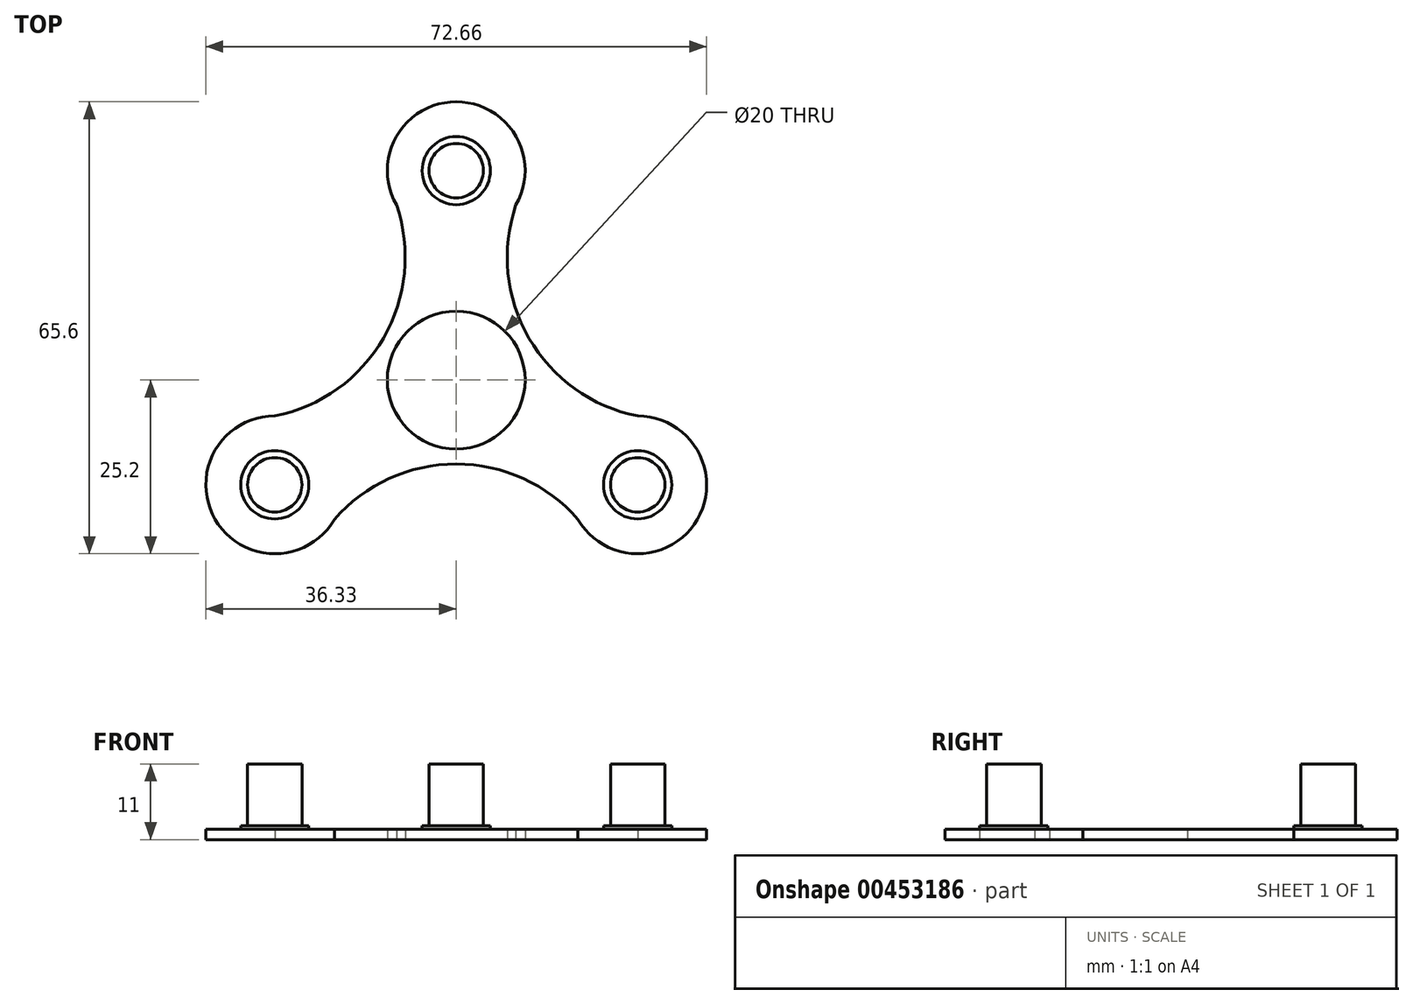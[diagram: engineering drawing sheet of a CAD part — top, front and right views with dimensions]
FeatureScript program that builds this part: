
annotation { "Feature Type Name" : "Feature", "Feature Type Description" : "" }
export const myFeature = defineFeature(function(context is Context, id is Id, definition is map)
    precondition{}
    {
        {
            var Q0;
            Q0=qCreatedBy(makeId("Top.planeOp"),FACE);
            var sketch = newSketch(context, id + "F0", { "sketchPlane" : qUnion([Q0])});
            skCircle(sketch, "E0", {"center": v(0, 0) * mm, "radius": 10 * mm});
            skLineSegment(sketch, "E1", {"start": v(0, 0) * mm, "end": v(0, 30.4) * mm});
            skCircle(sketch, "E2", {"center": v(0, 30.4) * mm, "radius": 3.95 * mm});
            skCircle(sketch, "E3.0", {"center": v(0, 30.4) * mm, "radius": 4.95 * mm});
            skCircle(sketch, "E4", {"center": v(0, 30.4) * mm, "radius": 10 * mm});
            skLineSegment(sketch, "E5", {"start": v(0, 30.4) * mm, "end": v(-8.66, 25.4) * mm});
            skLineSegment(sketch, "E6.MirrorCS", {"start": v(0, 30.4) * mm, "end": v(8.66, 25.4) * mm});
            skCircle(sketch, "E7.1.0", {"center": v(26.33, -15.2) * mm, "radius": 3.95 * mm});
            skLineSegment(sketch, "E7.1.1", {"start": v(26.33, -15.2) * mm, "end": v(17.67, -20.2) * mm});
            skLineSegment(sketch, "E7.1.2", {"start": v(26.33, -15.2) * mm, "end": v(26.33, -5.2) * mm});
            skCircle(sketch, "E7.1.3", {"center": v(26.33, -15.2) * mm, "radius": 4.95 * mm});
            skCircle(sketch, "E7.1.4", {"center": v(26.33, -15.2) * mm, "radius": 10 * mm});
            skCircle(sketch, "E7.2.0", {"center": v(-26.33, -15.2) * mm, "radius": 3.95 * mm});
            skLineSegment(sketch, "E7.2.1", {"start": v(-26.33, -15.2) * mm, "end": v(-26.33, -5.2) * mm});
            skLineSegment(sketch, "E7.2.2", {"start": v(-26.33, -15.2) * mm, "end": v(-17.67, -20.2) * mm});
            skCircle(sketch, "E7.2.3", {"center": v(-26.33, -15.2) * mm, "radius": 4.95 * mm});
            skCircle(sketch, "E7.2.4", {"center": v(-26.33, -15.2) * mm, "radius": 10 * mm});
            skLineSegment(sketch, "E7.anchor1", {"start": v(0, 0) * mm, "end": v(-8.66, 25.4) * mm, "construction": true});
            skLineSegment(sketch, "E7.anchor2", {"start": v(0, 0) * mm, "end": v(-17.67, -20.2) * mm, "construction": true});
            skArc(sketch, "E8", {"start": v(-26.33, -5.2) * mm, "mid": v(-10.55, 6.1) * mm, "end": v(-8.66, 25.4) * mm});
            skArc(sketch, "E9.1.0", {"start": v(17.67, -20.2) * mm, "mid": v(0, -12.18) * mm, "end": v(-17.67, -20.2) * mm});
            skArc(sketch, "E9.2.0", {"start": v(8.66, 25.4) * mm, "mid": v(10.55, 6.1) * mm, "end": v(26.33, -5.2) * mm});
            skSolve(sketch);
        }
        {
            var Q0;
            {var subQ0=sQuery(id+"F0.wireOp",EDGE,"E5");var subQ1=sQuery(id+"F0.wireOp",EDGE,"E3.0");var subQ2=makeQuery(id+"F0.imprint","INTERSECT",VERTEX,{"derivedFrom":[subQ1,subQ0]});Q0=makeQuery(id+"F0.imprint","IMPRINT",FACE,{"disambiguationData":[TD([[makeQuery(id+"F0.imprint","IMPRINT",EDGE,{"disambiguationData":[TD([[subQ2,1.0]])],"derivedFrom":subQ1}),-1.0]])]});}
            var Q1;
            {var subQ0=sQuery(id+"F0.wireOp",EDGE,"E4");var subQ1=sQuery(id+"F0.wireOp",EDGE,"E1");var subQ2=makeQuery(id+"F0.imprint","INTERSECT",VERTEX,{"derivedFrom":[subQ1,subQ0]});Q1=makeQuery(id+"F0.imprint","IMPRINT",FACE,{"disambiguationData":[TD([[makeQuery(id+"F0.imprint","IMPRINT",EDGE,{"disambiguationData":[TD([[subQ2,-1.0]])],"derivedFrom":subQ1}),-1.0]])]});}
            var Q2;
            {var subQ0=sQuery(id+"F0.wireOp",EDGE,"E4");var subQ1=sQuery(id+"F0.wireOp",EDGE,"E1");var subQ2=makeQuery(id+"F0.imprint","INTERSECT",VERTEX,{"derivedFrom":[subQ1,subQ0]});Q2=makeQuery(id+"F0.imprint","IMPRINT",FACE,{"disambiguationData":[TD([[makeQuery(id+"F0.imprint","IMPRINT",EDGE,{"disambiguationData":[TD([[subQ2,-1.0]])],"derivedFrom":subQ1}),1.0]])]});}
            var Q3;
            Q3=makeQuery(id+"F0.imprint","IMPRINT",FACE,{"disambiguationData":[TD([[makeQuery(id+"F0.imprint","IMPRINT",EDGE,{"derivedFrom":sQuery(id+"F0.wireOp",EDGE,"E0")}),-1.0]])]});
            var Q4;
            {var subQ1=sQuery(id+"F0.wireOp",EDGE,"E7.2.1");var subQ3=sQuery(id+"F0.wireOp",EDGE,"E7.2.3");var subQ4=makeQuery(id+"F0.imprint","INTERSECT",VERTEX,{"derivedFrom":[subQ1,subQ3]});Q4=makeQuery(id+"F0.imprint","IMPRINT",FACE,{"disambiguationData":[TD([[makeQuery(id+"F0.imprint","IMPRINT",EDGE,{"disambiguationData":[TD([[subQ4,1.0]])],"derivedFrom":subQ3}),-1.0]])]});}
            var Q5;
            {var subQ1=sQuery(id+"F0.wireOp",EDGE,"E7.2.1");var subQ3=sQuery(id+"F0.wireOp",EDGE,"E7.2.3");var subQ4=makeQuery(id+"F0.imprint","INTERSECT",VERTEX,{"derivedFrom":[subQ1,subQ3]});Q5=makeQuery(id+"F0.imprint","IMPRINT",FACE,{"disambiguationData":[TD([[makeQuery(id+"F0.imprint","IMPRINT",EDGE,{"disambiguationData":[TD([[subQ4,-1.0]])],"derivedFrom":subQ3}),-1.0]])]});}
            var Q6;
            {var subQ1=sQuery(id+"F0.wireOp",EDGE,"E7.1.1");var subQ3=sQuery(id+"F0.wireOp",EDGE,"E7.1.3");var subQ4=makeQuery(id+"F0.imprint","INTERSECT",VERTEX,{"derivedFrom":[subQ1,subQ3]});Q6=makeQuery(id+"F0.imprint","IMPRINT",FACE,{"disambiguationData":[TD([[makeQuery(id+"F0.imprint","IMPRINT",EDGE,{"disambiguationData":[TD([[subQ4,-1.0]])],"derivedFrom":subQ3}),-1.0]])]});}
            var Q7;
            {var subQ1=sQuery(id+"F0.wireOp",EDGE,"E7.1.1");var subQ3=sQuery(id+"F0.wireOp",EDGE,"E7.1.3");var subQ4=makeQuery(id+"F0.imprint","INTERSECT",VERTEX,{"derivedFrom":[subQ1,subQ3]});Q7=makeQuery(id+"F0.imprint","IMPRINT",FACE,{"disambiguationData":[TD([[makeQuery(id+"F0.imprint","IMPRINT",EDGE,{"disambiguationData":[TD([[subQ4,1.0]])],"derivedFrom":subQ3}),-1.0]])]});}
            extrude(context, id + "F1", {"entities" : qUnion([Q0, Q1, Q2, Q3, Q4, Q5, Q6, Q7]), "depth" : 1.5 * mm});
        }
        {
            var Q0;
            {var subQ0=sQuery(id+"F0.wireOp",EDGE,"E5");var subQ1=sQuery(id+"F0.wireOp",EDGE,"E2");var subQ2=makeQuery(id+"F0.imprint","INTERSECT",VERTEX,{"derivedFrom":[subQ1,subQ0]});Q0=makeQuery(id+"F0.imprint","IMPRINT",FACE,{"disambiguationData":[TD([[makeQuery(id+"F0.imprint","IMPRINT",EDGE,{"disambiguationData":[TD([[subQ2,1.0]])],"derivedFrom":subQ1}),-1.0]])]});}
            var Q1;
            {var subQ0=sQuery(id+"F0.wireOp",EDGE,"E3.0");var subQ1=sQuery(id+"F0.wireOp",EDGE,"E1");var subQ2=makeQuery(id+"F0.imprint","INTERSECT",VERTEX,{"derivedFrom":[subQ1,subQ0]});Q1=makeQuery(id+"F0.imprint","IMPRINT",FACE,{"disambiguationData":[TD([[makeQuery(id+"F0.imprint","IMPRINT",EDGE,{"disambiguationData":[TD([[subQ2,-1.0]])],"derivedFrom":subQ1}),1.0]])]});}
            var Q2;
            {var subQ0=sQuery(id+"F0.wireOp",EDGE,"E3.0");var subQ1=sQuery(id+"F0.wireOp",EDGE,"E1");var subQ2=makeQuery(id+"F0.imprint","INTERSECT",VERTEX,{"derivedFrom":[subQ1,subQ0]});Q2=makeQuery(id+"F0.imprint","IMPRINT",FACE,{"disambiguationData":[TD([[makeQuery(id+"F0.imprint","IMPRINT",EDGE,{"disambiguationData":[TD([[subQ2,-1.0]])],"derivedFrom":subQ1}),-1.0]])]});}
            var Q3;
            {var subQ0=sQuery(id+"F0.wireOp",EDGE,"E7.1.1");var subQ1=sQuery(id+"F0.wireOp",EDGE,"E7.1.0");var subQ2=makeQuery(id+"F0.imprint","INTERSECT",VERTEX,{"derivedFrom":[subQ1,subQ0]});Q3=makeQuery(id+"F0.imprint","IMPRINT",FACE,{"disambiguationData":[TD([[makeQuery(id+"F0.imprint","IMPRINT",EDGE,{"disambiguationData":[TD([[subQ2,1.0]])],"derivedFrom":subQ1}),-1.0]])]});}
            var Q4;
            {var subQ0=sQuery(id+"F0.wireOp",EDGE,"E7.1.1");var subQ1=sQuery(id+"F0.wireOp",EDGE,"E7.1.0");var subQ2=makeQuery(id+"F0.imprint","INTERSECT",VERTEX,{"derivedFrom":[subQ1,subQ0]});Q4=makeQuery(id+"F0.imprint","IMPRINT",FACE,{"disambiguationData":[TD([[makeQuery(id+"F0.imprint","IMPRINT",EDGE,{"disambiguationData":[TD([[subQ2,-1.0]])],"derivedFrom":subQ1}),-1.0]])]});}
            var Q5;
            {var subQ0=sQuery(id+"F0.wireOp",EDGE,"E7.2.1");var subQ1=sQuery(id+"F0.wireOp",EDGE,"E7.2.0");var subQ2=makeQuery(id+"F0.imprint","INTERSECT",VERTEX,{"derivedFrom":[subQ1,subQ0]});Q5=makeQuery(id+"F0.imprint","IMPRINT",FACE,{"disambiguationData":[TD([[makeQuery(id+"F0.imprint","IMPRINT",EDGE,{"disambiguationData":[TD([[subQ2,-1.0]])],"derivedFrom":subQ1}),-1.0]])]});}
            var Q6;
            {var subQ0=sQuery(id+"F0.wireOp",EDGE,"E7.2.1");var subQ1=sQuery(id+"F0.wireOp",EDGE,"E7.2.0");var subQ2=makeQuery(id+"F0.imprint","INTERSECT",VERTEX,{"derivedFrom":[subQ1,subQ0]});Q6=makeQuery(id+"F0.imprint","IMPRINT",FACE,{"disambiguationData":[TD([[makeQuery(id+"F0.imprint","IMPRINT",EDGE,{"disambiguationData":[TD([[subQ2,1.0]])],"derivedFrom":subQ1}),-1.0]])]});}
            extrude(context, id + "F2", {"entities" : qUnion([Q0, Q1, Q2, Q3, Q4, Q5, Q6]), "operationType" : NewBodyOperationType.ADD, "depth" : 2 * mm});
        }
        {
            var Q0;
            {var subQ0=sQuery(id+"F0.wireOp",EDGE,"E5");var subQ1=sQuery(id+"F0.wireOp",EDGE,"E2");var subQ2=makeQuery(id+"F0.imprint","INTERSECT",VERTEX,{"derivedFrom":[subQ1,subQ0]});Q0=makeQuery(id+"F0.imprint","IMPRINT",FACE,{"disambiguationData":[TD([[makeQuery(id+"F0.imprint","IMPRINT",EDGE,{"disambiguationData":[TD([[subQ2,1.0]])],"derivedFrom":subQ1}),1.0]])]});}
            var Q1;
            {var subQ1=sQuery(id+"F0.wireOp",EDGE,"E1");var subQ3=sQuery(id+"F0.wireOp",EDGE,"E2");var subQ4=makeQuery(id+"F0.imprint","INTERSECT",VERTEX,{"derivedFrom":[subQ1,subQ3]});Q1=makeQuery(id+"F0.imprint","IMPRINT",FACE,{"disambiguationData":[TD([[makeQuery(id+"F0.imprint","IMPRINT",EDGE,{"disambiguationData":[TD([[subQ4,1.0]])],"derivedFrom":subQ3}),1.0]])]});}
            var Q2;
            {var subQ1=sQuery(id+"F0.wireOp",EDGE,"E1");var subQ3=sQuery(id+"F0.wireOp",EDGE,"E2");var subQ4=makeQuery(id+"F0.imprint","INTERSECT",VERTEX,{"derivedFrom":[subQ1,subQ3]});Q2=makeQuery(id+"F0.imprint","IMPRINT",FACE,{"disambiguationData":[TD([[makeQuery(id+"F0.imprint","IMPRINT",EDGE,{"disambiguationData":[TD([[subQ4,-1.0]])],"derivedFrom":subQ3}),1.0]])]});}
            var Q3;
            {var subQ0=sQuery(id+"F0.wireOp",EDGE,"E7.2.1");var subQ1=sQuery(id+"F0.wireOp",EDGE,"E7.2.0");var subQ2=makeQuery(id+"F0.imprint","INTERSECT",VERTEX,{"derivedFrom":[subQ1,subQ0]});Q3=makeQuery(id+"F0.imprint","IMPRINT",FACE,{"disambiguationData":[TD([[makeQuery(id+"F0.imprint","IMPRINT",EDGE,{"disambiguationData":[TD([[subQ2,1.0]])],"derivedFrom":subQ1}),1.0]])]});}
            var Q4;
            {var subQ0=sQuery(id+"F0.wireOp",EDGE,"E7.2.1");var subQ1=sQuery(id+"F0.wireOp",EDGE,"E7.2.0");var subQ2=makeQuery(id+"F0.imprint","INTERSECT",VERTEX,{"derivedFrom":[subQ1,subQ0]});Q4=makeQuery(id+"F0.imprint","IMPRINT",FACE,{"disambiguationData":[TD([[makeQuery(id+"F0.imprint","IMPRINT",EDGE,{"disambiguationData":[TD([[subQ2,-1.0]])],"derivedFrom":subQ1}),1.0]])]});}
            var Q5;
            {var subQ0=sQuery(id+"F0.wireOp",EDGE,"E7.1.1");var subQ1=sQuery(id+"F0.wireOp",EDGE,"E7.1.0");var subQ2=makeQuery(id+"F0.imprint","INTERSECT",VERTEX,{"derivedFrom":[subQ1,subQ0]});Q5=makeQuery(id+"F0.imprint","IMPRINT",FACE,{"disambiguationData":[TD([[makeQuery(id+"F0.imprint","IMPRINT",EDGE,{"disambiguationData":[TD([[subQ2,1.0]])],"derivedFrom":subQ1}),1.0]])]});}
            var Q6;
            {var subQ0=sQuery(id+"F0.wireOp",EDGE,"E7.1.1");var subQ1=sQuery(id+"F0.wireOp",EDGE,"E7.1.0");var subQ2=makeQuery(id+"F0.imprint","INTERSECT",VERTEX,{"derivedFrom":[subQ1,subQ0]});Q6=makeQuery(id+"F0.imprint","IMPRINT",FACE,{"disambiguationData":[TD([[makeQuery(id+"F0.imprint","IMPRINT",EDGE,{"disambiguationData":[TD([[subQ2,-1.0]])],"derivedFrom":subQ1}),1.0]])]});}
            extrude(context, id + "F3", {"entities" : qUnion([Q0, Q1, Q2, Q3, Q4, Q5, Q6]), "operationType" : NewBodyOperationType.ADD, "depth" : 11 * mm});
        }
    });
